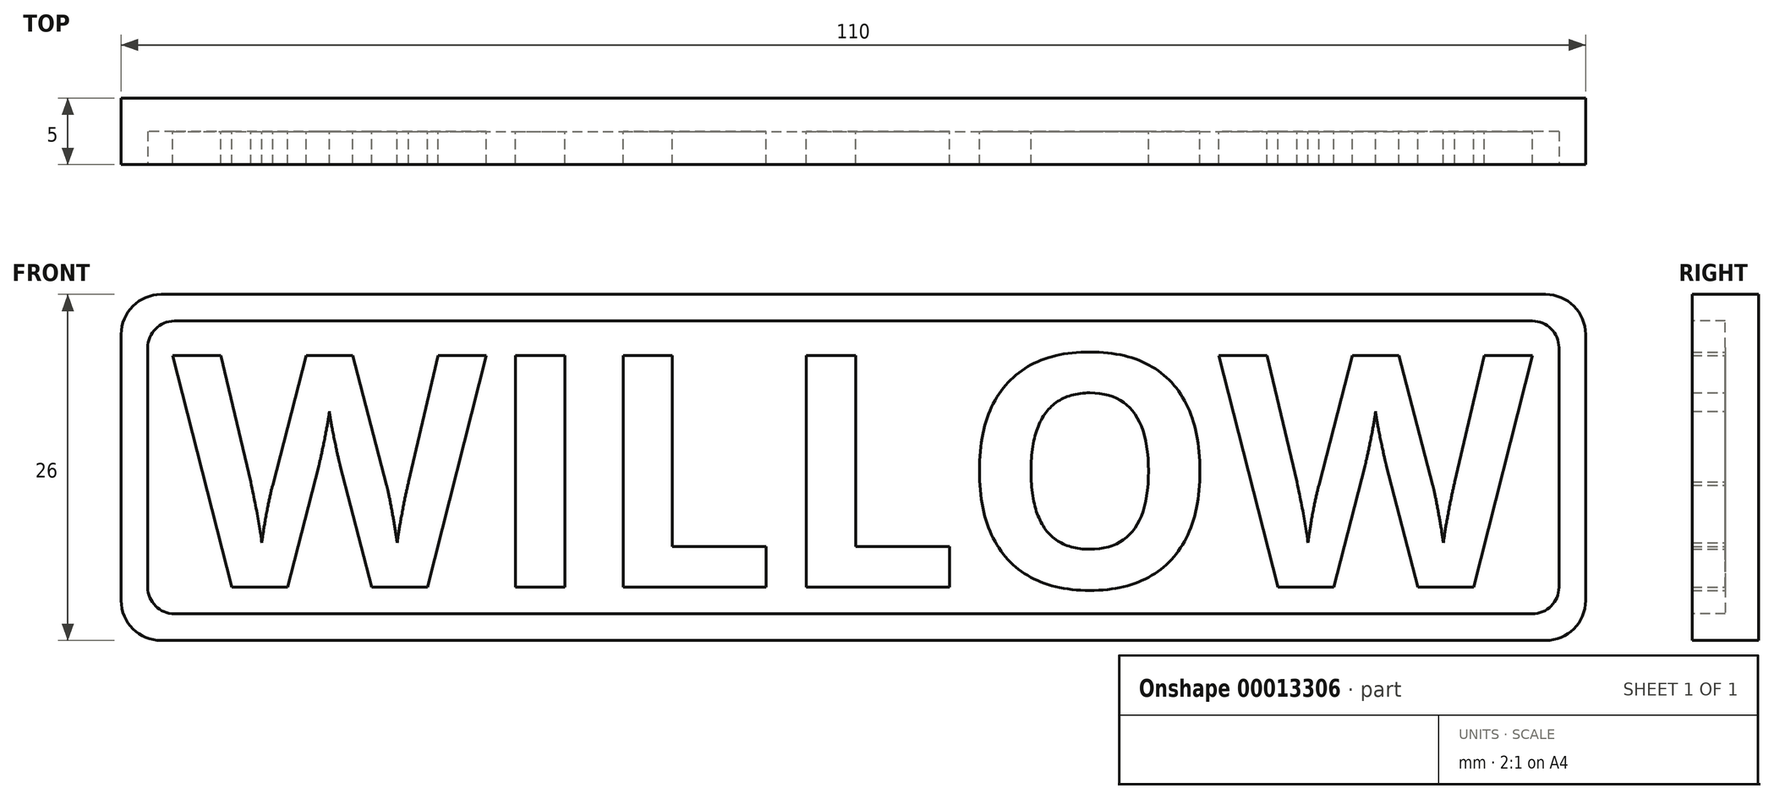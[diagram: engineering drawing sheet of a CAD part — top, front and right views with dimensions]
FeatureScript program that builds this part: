
annotation { "Feature Type Name" : "Feature", "Feature Type Description" : "" }
export const myFeature = defineFeature(function(context is Context, id is Id, definition is map)
    precondition{}
    {
        {
            var Q0;
            Q0=qCreatedBy(makeId("Front.planeOp"),FACE);
            var sketch = newSketch(context, id + "F0", { "sketchPlane" : qUnion([Q0])});
            skLineSegment(sketch, "E0.bottom", {"start": v(3, 0) * mm, "end": v(107, 0) * mm});
            skLineSegment(sketch, "E0.top", {"start": v(3, 26) * mm, "end": v(107, 26) * mm});
            skLineSegment(sketch, "E0.left", {"start": v(0, 3) * mm, "end": v(0, 23) * mm});
            skLineSegment(sketch, "E0.right", {"start": v(110, 3) * mm, "end": v(110, 23) * mm});
            skPoint(sketch, "E1.visualSharp", {"position": v(0, 26) * mm});
            skArc(sketch, "E1.filletArc", {"start": v(3, 26) * mm, "mid": v(0.88, 25.12) * mm, "end": v(0, 23) * mm});
            skPoint(sketch, "E2.visualSharp", {"position": v(110, 26) * mm});
            skArc(sketch, "E2.filletArc", {"start": v(110, 23) * mm, "mid": v(109.12, 25.12) * mm, "end": v(107, 26) * mm});
            skPoint(sketch, "E3.visualSharp", {"position": v(110, 0) * mm});
            skArc(sketch, "E3.filletArc", {"start": v(107, 0) * mm, "mid": v(109.12, 0.88) * mm, "end": v(110, 3) * mm});
            skPoint(sketch, "E4.visualSharp", {"position": v(0, 0) * mm});
            skArc(sketch, "E4.filletArc", {"start": v(0, 3) * mm, "mid": v(0.88, 0.88) * mm, "end": v(3, 0) * mm});
            skSolve(sketch);
        }
        {
            var Q0;
            Q0 = qSketchRegion(id + "F0", true);
            extrude(context, id + "F1", {"entities" : qUnion([Q0]), "depth" : 5 * mm});
        }
        {
            var Q0;
            Q0=makeQuery(id+"F1.opExtrude","CAP_FACE",FACE,{"disambiguationData":[OSD([sQuery(id+"F0.wireOp",EDGE,"E0.bottom"),sQuery(id+"F0.wireOp",EDGE,"E0.top"),sQuery(id+"F0.wireOp",EDGE,"E0.left"),sQuery(id+"F0.wireOp",EDGE,"E0.right"),sQuery(id+"F0.wireOp",EDGE,"E1.filletArc"),sQuery(id+"F0.wireOp",EDGE,"E2.filletArc"),sQuery(id+"F0.wireOp",EDGE,"E3.filletArc"),sQuery(id+"F0.wireOp",EDGE,"E4.filletArc")])],"isStart":false});
            var sketch = newSketch(context, id + "F2", { "sketchPlane" : qUnion([Q0])});
            skLineSegment(sketch, "E5.bottom", {"start": v(4, 24) * mm, "end": v(106, 24) * mm});
            skLineSegment(sketch, "E5.top", {"start": v(4, 2) * mm, "end": v(106, 2) * mm});
            skLineSegment(sketch, "E5.left", {"start": v(2, 22) * mm, "end": v(2, 4) * mm});
            skLineSegment(sketch, "E5.right", {"start": v(108, 22) * mm, "end": v(108, 4) * mm});
            skPoint(sketch, "E6.visualSharp", {"position": v(2, 24) * mm});
            skArc(sketch, "E6.filletArc", {"start": v(4, 24) * mm, "mid": v(2.59, 23.41) * mm, "end": v(2, 22) * mm});
            skPoint(sketch, "E7.visualSharp", {"position": v(108, 24) * mm});
            skArc(sketch, "E7.filletArc", {"start": v(108, 22) * mm, "mid": v(107.41, 23.41) * mm, "end": v(106, 24) * mm});
            skPoint(sketch, "E8.visualSharp", {"position": v(108, 2) * mm});
            skArc(sketch, "E8.filletArc", {"start": v(106, 2) * mm, "mid": v(107.41, 2.59) * mm, "end": v(108, 4) * mm});
            skPoint(sketch, "E9.visualSharp", {"position": v(2, 2) * mm});
            skArc(sketch, "E9.filletArc", {"start": v(2, 4) * mm, "mid": v(2.59, 2.59) * mm, "end": v(4, 2) * mm});
            skSolve(sketch);
        }
        {
            var Q0;
            Q0 = qSketchRegion(id + "F2", true);
            extrude(context, id + "F3", {"entities" : qUnion([Q0]), "operationType" : NewBodyOperationType.REMOVE, "oppositeDirection" : true, "depth" : 2.5 * mm});
        }
        {
            var Q0;
            Q0=makeQuery(id+"F3.boolean.opBoolean","COPY",FACE,{"derivedFrom":makeQuery(id+"F3.opExtrude","CAP_FACE",FACE,{"disambiguationData":[OSD([sQuery(id+"F2.wireOp",EDGE,"E5.bottom"),sQuery(id+"F2.wireOp",EDGE,"E5.top"),sQuery(id+"F2.wireOp",EDGE,"E5.left"),sQuery(id+"F2.wireOp",EDGE,"E5.right"),sQuery(id+"F2.wireOp",EDGE,"E6.filletArc"),sQuery(id+"F2.wireOp",EDGE,"E7.filletArc"),sQuery(id+"F2.wireOp",EDGE,"E8.filletArc"),sQuery(id+"F2.wireOp",EDGE,"E9.filletArc")])],"isStart":false})});
            var sketch = newSketch(context, id + "F4", { "sketchPlane" : qUnion([Q0])});
            skText(sketch, "E10", { "text": "WILLOW", "fontName": "OpenSans-Bold.ttf"});
            const initialGuessF4  = {"E10": [0.00387, 0.004, 1, 0, 0.01755]};
            skSetInitialGuess(sketch, initialGuessF4);
            skSolve(sketch);
        }
        {
            var Q0;
            Q0 = qSketchRegion(id + "F4", true);
            extrude(context, id + "F5", {"entities" : qUnion([Q0]), "operationType" : NewBodyOperationType.ADD, "depth" : 2.5 * mm});
        }
    });
